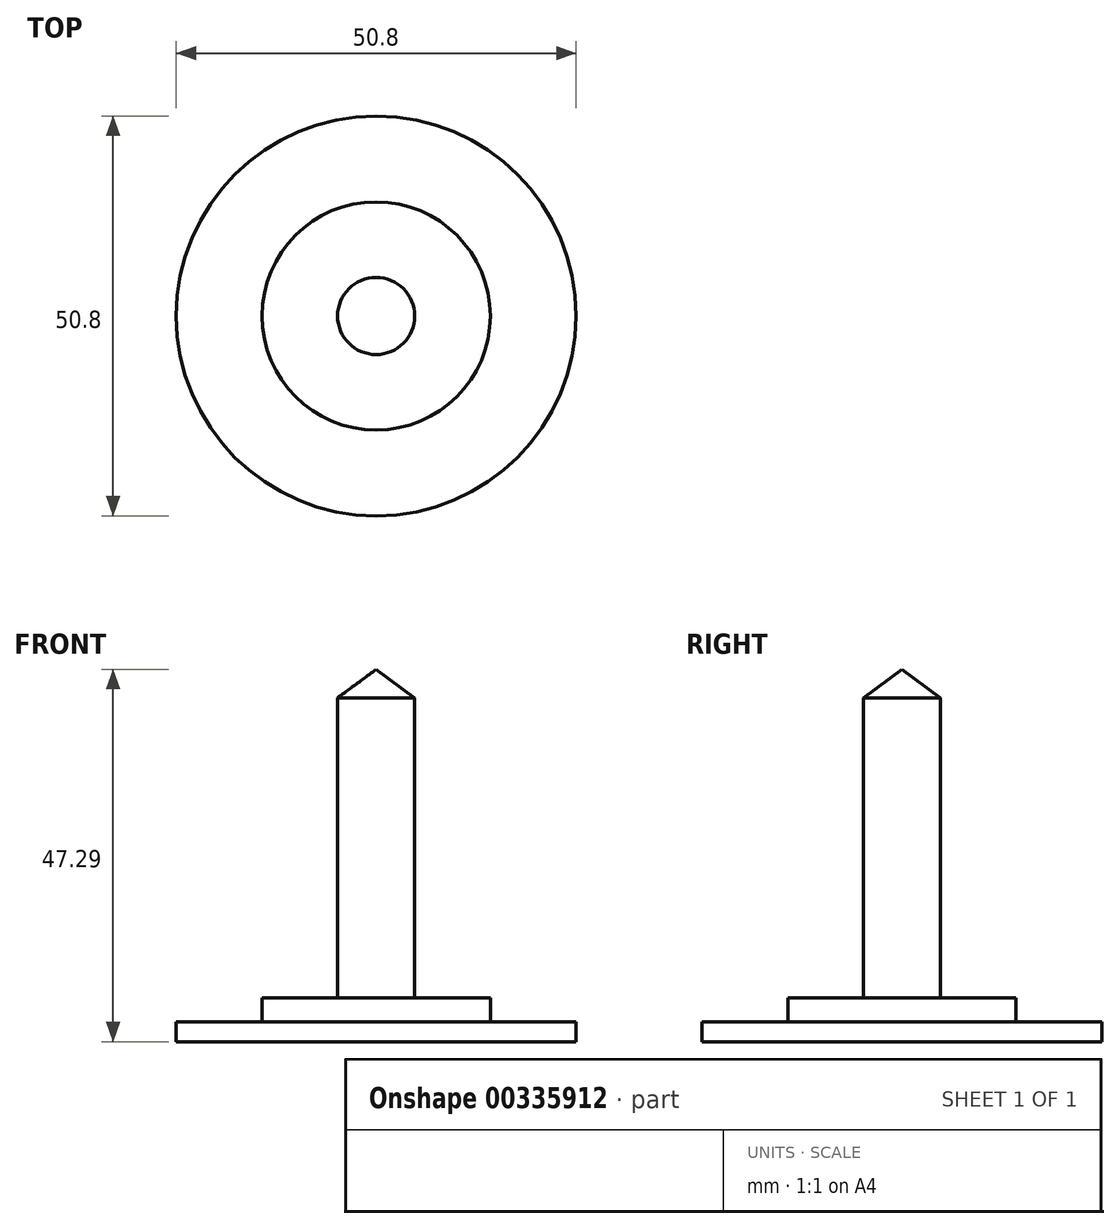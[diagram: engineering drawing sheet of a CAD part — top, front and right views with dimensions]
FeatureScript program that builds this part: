
annotation { "Feature Type Name" : "Feature", "Feature Type Description" : "" }
export const myFeature = defineFeature(function(context is Context, id is Id, definition is map)
    precondition{}
    {
        {
            var Q0;
            Q0=qCreatedBy(makeId("Front.planeOp"),FACE);
            var sketch = newSketch(context, id + "F0", { "sketchPlane" : qUnion([Q0])});
            skLineSegment(sketch, "E0", {"start": v(0, 0) * mm, "end": v(25.4, 0) * mm});
            skLineSegment(sketch, "E1", {"start": v(25.4, 0) * mm, "end": v(25.4, 2.54) * mm});
            skLineSegment(sketch, "E2", {"start": v(14.5, 2.54) * mm, "end": v(14.5, 5.58) * mm});
            skLineSegment(sketch, "E3", {"start": v(14.5, 5.58) * mm, "end": v(4.9, 5.58) * mm});
            skLineSegment(sketch, "E4", {"start": v(4.9, 5.58) * mm, "end": v(4.9, 43.68) * mm});
            skFitSpline(sketch, "E5", {"points": [v(4.9, 43.68) * mm, v(21.8, 51.9) * mm, v(21.8, 52.47) * mm, v(30.72, 69.17) * mm, v(38.5, 159.87) * mm, v(38.2, 160.45) * mm], "startDerivative": vector(111.63, 48) * mm, "endDerivative": vector(-7.42, 4.6) * mm});
            skFitSpline(sketch, "E6", {"points": [v(4.9, 47.29) * mm, v(18.05, 55.35) * mm, v(19.78, 58.23) * mm, v(26.4, 71.19) * mm, v(33.6, 160.16) * mm, v(33.89, 160.16) * mm], "startDerivative": vector(83.08, 43.47) * mm, "endDerivative": vector(10.68, -7.3) * mm});
            skLineSegment(sketch, "E7", {"start": v(33.79, 160.23) * mm, "end": v(38.5, 159.87) * mm});
            skLineSegment(sketch, "E8", {"start": v(4.9, 47.29) * mm, "end": v(2.21, 47.29) * mm});
            skLineSegment(sketch, "E9", {"start": v(2.21, 47.29) * mm, "end": v(0, 47.29) * mm});
            skLineSegment(sketch, "E10", {"start": v(0, 47.29) * mm, "end": v(4.9, 43.68) * mm});
            skLineSegment(sketch, "E11", {"start": v(0, 47.29) * mm, "end": v(0, 0) * mm});
            skLineSegment(sketch, "E12", {"start": v(14.5, 2.54) * mm, "end": v(25.4, 2.54) * mm});
            skSolve(sketch);
        }
        {
            var Q0;
            Q0=makeQuery(id+"F0.imprint","IMPRINT",FACE,{"disambiguationData":[TD([[makeQuery(id+"F0.imprint","IMPRINT",EDGE,{"derivedFrom":sQuery(id+"F0.wireOp",EDGE,"E0")}),1.0]])]});
            var Q1;
            Q1=sQuery(id+"F0.wireOp",EDGE,"E11");
            revolve(context, id + "F1", {"entities" : qUnion([Q0]), "axis" : qUnion([Q1]), "revolveType" : RevolveType.FULL});
        }
    });
